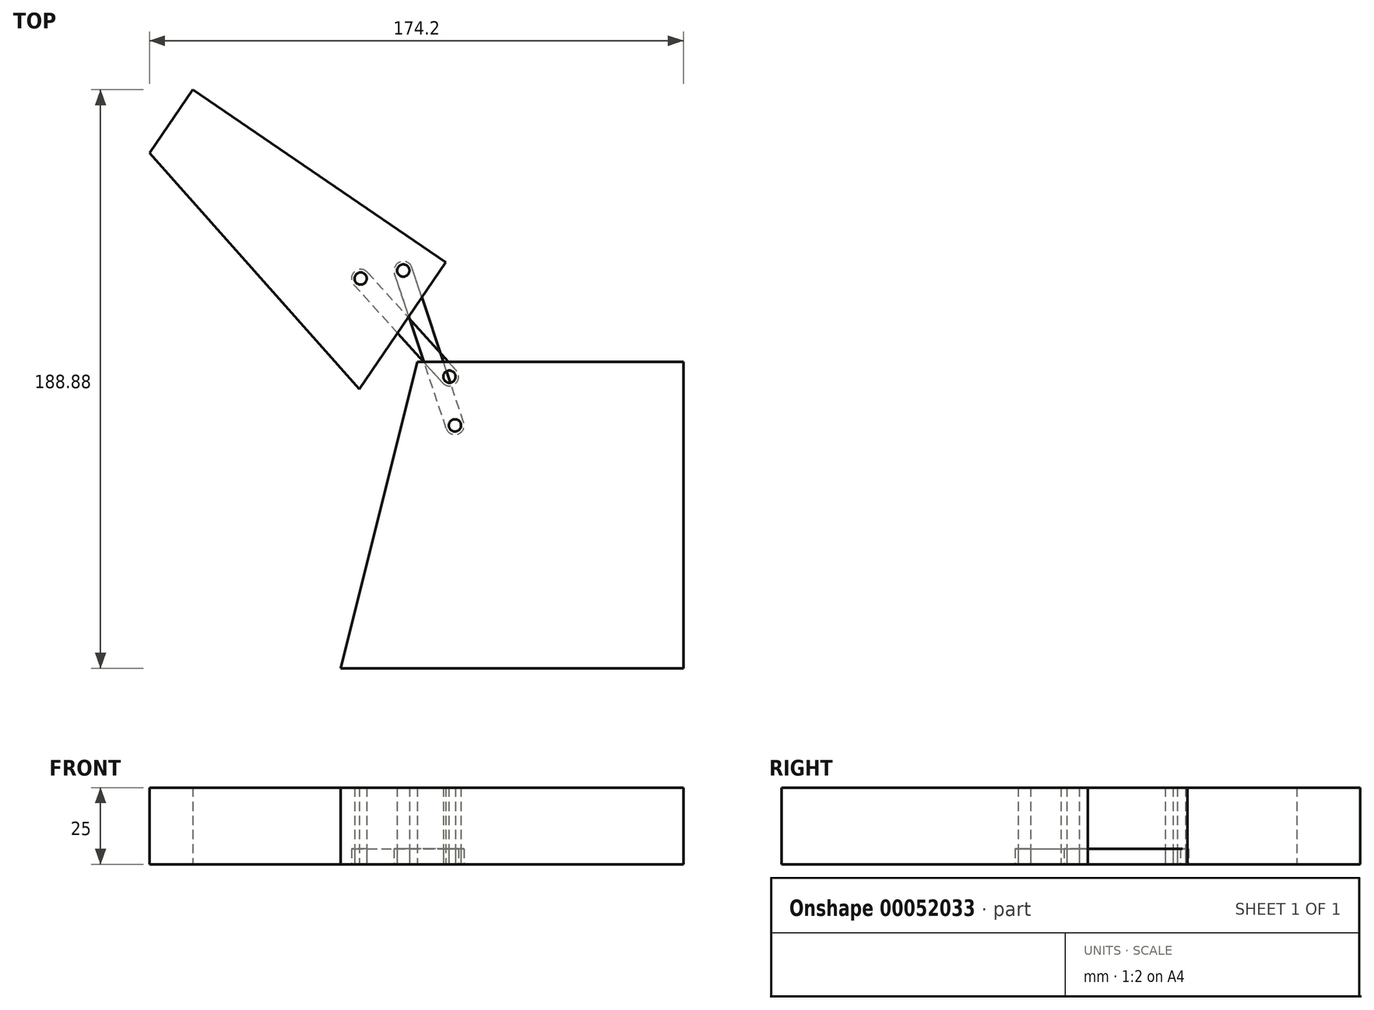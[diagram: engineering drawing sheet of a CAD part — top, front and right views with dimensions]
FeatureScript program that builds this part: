
annotation { "Feature Type Name" : "Feature", "Feature Type Description" : "" }
export const myFeature = defineFeature(function(context is Context, id is Id, definition is map)
    precondition{}
    {
        {
            var Q0;
            Q0=qCreatedBy(makeId("Top.planeOp"),FACE);
            var sketch = newSketch(context, id + "F0", { "sketchPlane" : qUnion([Q0])});
            skLineSegment(sketch, "E0.bottom", {"start": v(50, 0) * mm, "end": v(0, 0) * mm});
            skLineSegment(sketch, "E0.top", {"start": v(50, 100) * mm, "end": v(25, 100) * mm});
            skLineSegment(sketch, "E0.left", {"start": v(50, 0) * mm, "end": v(50, 100) * mm});
            skLineSegment(sketch, "E0.right", {"start": v(0, 0) * mm, "end": v(25, 100) * mm});
            skPoint(sketch, "E1", {"position": v(40, 10) * mm});
            skPoint(sketch, "E2", {"position": v(30, 20) * mm});
            skLineSegment(sketch, "E3.right", {"start": v(-34.75, -8.8) * mm, "end": v(-103.23, 68.24) * mm});
            skLineSegment(sketch, "E3.left", {"start": v(-6.55, 32.48) * mm, "end": v(-89.13, 88.88) * mm});
            skLineSegment(sketch, "E3.top", {"start": v(-89.13, 88.88) * mm, "end": v(-103.23, 68.24) * mm});
            skPoint(sketch, "E4", {"position": v(-20.45, 29.87) * mm});
            skPoint(sketch, "E5", {"position": v(-34.35, 27.25) * mm});
            skLineSegment(sketch, "E3.bottom", {"start": v(-6.55, 32.48) * mm, "end": v(-34.75, -8.8) * mm});
            skPoint(sketch, "E6", {"position": v(-55.82, -10) * mm});
            skPoint(sketch, "E7", {"position": v(-45.82, -20) * mm});
            skLineSegment(sketch, "E8.left", {"start": v(-65.82, 0) * mm, "end": v(-65.82, -100) * mm});
            skLineSegment(sketch, "E8.top", {"start": v(-65.82, -100) * mm, "end": v(-40.82, -100) * mm});
            skLineSegment(sketch, "E8.bottom", {"start": v(-65.82, 0) * mm, "end": v(-15.82, 0) * mm});
            skLineSegment(sketch, "E9", {"start": v(40, 10) * mm, "end": v(-20.45, 29.87) * mm, "construction": true});
            skLineSegment(sketch, "E10", {"start": v(-20.45, 29.87) * mm, "end": v(-55.82, -10) * mm, "construction": true});
            skLineSegment(sketch, "E11", {"start": v(30, 20) * mm, "end": v(-34.35, 27.25) * mm, "construction": true});
            skLineSegment(sketch, "E12", {"start": v(-34.35, 27.25) * mm, "end": v(-45.82, -20) * mm, "construction": true});
            skPoint(sketch, "E13", {"position": v(-38.13, 9.93) * mm});
            skPoint(sketch, "E14", {"position": v(9.78, 19.93) * mm});
            skLineSegment(sketch, "E15", {"start": v(-38.13, 9.93) * mm, "end": v(30.36, -50.84) * mm, "construction": true});
            skLineSegment(sketch, "E16", {"start": v(9.78, 19.93) * mm, "end": v(-26.41, -90.18) * mm, "construction": true});
            skPoint(sketch, "E17", {"position": v(-40.08, 3.62) * mm});
            skPoint(sketch, "E18", {"position": v(-2.17, 23.62) * mm});
            skLineSegment(sketch, "E19", {"start": v(-40.08, 3.62) * mm, "end": v(126.82, -36.9) * mm, "construction": true});
            skLineSegment(sketch, "E20", {"start": v(-2.17, 23.62) * mm, "end": v(-9.46, -41.02) * mm, "construction": true});
            skLineSegment(sketch, "E21", {"start": v(-15.82, 0) * mm, "end": v(-40.82, -100) * mm});
            skLineSegment(sketch, "E22", {"start": v(-40.82, -100) * mm, "end": v(70.97, -100) * mm});
            skLineSegment(sketch, "E23", {"start": v(70.97, -100) * mm, "end": v(70.97, 0) * mm});
            skLineSegment(sketch, "E24", {"start": v(70.97, 0) * mm, "end": v(-15.82, 0) * mm});
            skCircle(sketch, "E25", {"center": v(-20.45, 29.87) * mm, "radius": 2 * mm});
            skCircle(sketch, "E26", {"center": v(-34.35, 27.25) * mm, "radius": 3 * mm});
            skCircle(sketch, "E27", {"center": v(-20.45, 29.87) * mm, "radius": 3 * mm});
            skPoint(sketch, "E28", {"position": v(-5.38, -4.8) * mm});
            skPoint(sketch, "E29", {"position": v(-3.59, -20.72) * mm});
            skCircle(sketch, "E30", {"center": v(-34.35, 27.25) * mm, "radius": 2 * mm});
            skCircle(sketch, "E31", {"center": v(-5.38, -4.8) * mm, "radius": 2 * mm});
            skCircle(sketch, "E32", {"center": v(-5.38, -4.8) * mm, "radius": 3 * mm});
            skCircle(sketch, "E33", {"center": v(-3.59, -20.72) * mm, "radius": 2 * mm});
            skCircle(sketch, "E34", {"center": v(-3.59, -20.72) * mm, "radius": 3 * mm});
            skLineSegment(sketch, "E35", {"start": v(-36.57, 25.24) * mm, "end": v(-7.6, -6.82) * mm});
            skLineSegment(sketch, "E36", {"start": v(-32.12, 29.26) * mm, "end": v(-3.15, -2.8) * mm});
            skLineSegment(sketch, "E37", {"start": v(-0.74, -19.77) * mm, "end": v(-17.6, 30.81) * mm});
            skLineSegment(sketch, "E38", {"start": v(-6.43, -21.67) * mm, "end": v(-23.3, 28.92) * mm});
            skSolve(sketch);
        }
        {
            var Q0;
            {var subQ3=sQuery(id+"F0.wireOp",EDGE,"E21");Q0=makeQuery(id+"F0.imprint","IMPRINT",FACE,{"disambiguationData":[TD([[makeQuery(id+"F0.imprint","IMPRINT",EDGE,{"derivedFrom":subQ3}),1.0]])]});}
            var Q1;
            Q1=makeQuery(id+"F0.imprint","IMPRINT",FACE,{"disambiguationData":[TD([[makeQuery(id+"F0.imprint","IMPRINT",EDGE,{"derivedFrom":sQuery(id+"F0.wireOp",EDGE,"E33")}),-1.0]])]});
            var Q2;
            {var subQ3=sQuery(id+"F0.wireOp",EDGE,"E32");var subQ5=sQuery(id+"F0.wireOp",EDGE,"E35");var subQ6=makeQuery(id+"F0.imprint","INTERSECT",VERTEX,{"derivedFrom":[subQ3,subQ5]});Q2=makeQuery(id+"F0.imprint","IMPRINT",FACE,{"disambiguationData":[TD([[makeQuery(id+"F0.imprint","IMPRINT",EDGE,{"disambiguationData":[TD([[subQ6,-1.0]])],"derivedFrom":subQ3}),-1.0]])]});}
            var Q3;
            {var subQ0=sQuery(id+"F0.wireOp",EDGE,"E37");var subQ1=sQuery(id+"F0.wireOp",EDGE,"E31");var subQ2=makeQuery(id+"F0.imprint","INTERSECT",VERTEX,{"disambiguationData":[OD(0.0)],"derivedFrom":[subQ1,subQ0]});Q3=makeQuery(id+"F0.imprint","IMPRINT",FACE,{"disambiguationData":[TD([[makeQuery(id+"F0.imprint","IMPRINT",EDGE,{"disambiguationData":[TD([[subQ2,1.0]])],"derivedFrom":subQ1}),-1.0]])]});}
            var Q4;
            {var subQ5=sQuery(id+"F0.wireOp",EDGE,"E37");var subQ7=sQuery(id+"F0.wireOp",EDGE,"E24");var subQ8=makeQuery(id+"F0.imprint","INTERSECT",VERTEX,{"derivedFrom":[subQ7,subQ5]});Q4=makeQuery(id+"F0.imprint","IMPRINT",FACE,{"disambiguationData":[TD([[makeQuery(id+"F0.imprint","IMPRINT",EDGE,{"disambiguationData":[TD([[subQ8,-1.0]])],"derivedFrom":subQ7}),1.0]])]});}
            var Q5;
            {var subQ0=sQuery(id+"F0.wireOp",EDGE,"E36");var subQ1=sQuery(id+"F0.wireOp",EDGE,"E24");var subQ2=makeQuery(id+"F0.imprint","INTERSECT",VERTEX,{"derivedFrom":[subQ1,subQ0]});Q5=makeQuery(id+"F0.imprint","IMPRINT",FACE,{"disambiguationData":[TD([[makeQuery(id+"F0.imprint","IMPRINT",EDGE,{"disambiguationData":[TD([[subQ2,-1.0]])],"derivedFrom":subQ1}),1.0]])]});}
            var Q6;
            {var subQ0=sQuery(id+"F0.wireOp",EDGE,"E37");var subQ1=sQuery(id+"F0.wireOp",EDGE,"E31");var subQ2=makeQuery(id+"F0.imprint","INTERSECT",VERTEX,{"disambiguationData":[OD(0.0)],"derivedFrom":[subQ1,subQ0]});Q6=makeQuery(id+"F0.imprint","IMPRINT",FACE,{"disambiguationData":[TD([[makeQuery(id+"F0.imprint","IMPRINT",EDGE,{"disambiguationData":[TD([[subQ2,-1.0]])],"derivedFrom":subQ1}),-1.0]])]});}
            var Q7;
            {var subQ0=sQuery(id+"F0.wireOp",EDGE,"E38");var subQ1=sQuery(id+"F0.wireOp",EDGE,"E24");var subQ2=makeQuery(id+"F0.imprint","INTERSECT",VERTEX,{"derivedFrom":[subQ1,subQ0]});Q7=makeQuery(id+"F0.imprint","IMPRINT",FACE,{"disambiguationData":[TD([[makeQuery(id+"F0.imprint","IMPRINT",EDGE,{"disambiguationData":[TD([[subQ2,-1.0]])],"derivedFrom":subQ1}),1.0]])]});}
            extrude(context, id + "F1", {"entities" : qUnion([Q0, Q1, Q2, Q3, Q4, Q5, Q6, Q7]), "depth" : 25 * mm});
        }
        {
            var Q0;
            {var subQ15=sQuery(id+"F0.wireOp",EDGE,"E3.left");Q0=makeQuery(id+"F0.imprint","IMPRINT",FACE,{"disambiguationData":[TD([[makeQuery(id+"F0.imprint","IMPRINT",EDGE,{"derivedFrom":subQ15}),1.0]])]});}
            var Q1;
            {var subQ0=sQuery(id+"F0.wireOp",EDGE,"E36");var subQ1=sQuery(id+"F0.wireOp",EDGE,"E3.bottom");var subQ2=makeQuery(id+"F0.imprint","INTERSECT",VERTEX,{"derivedFrom":[subQ1,subQ0]});Q1=makeQuery(id+"F0.imprint","IMPRINT",FACE,{"disambiguationData":[TD([[makeQuery(id+"F0.imprint","IMPRINT",EDGE,{"disambiguationData":[TD([[subQ2,-1.0]])],"derivedFrom":subQ1}),-1.0]])]});}
            var Q2;
            {var subQ0=sQuery(id+"F0.wireOp",EDGE,"E3.bottom");var subQ1=sQuery(id+"F0.wireOp",EDGE,"E3.right");var subQ2=makeQuery(id+"F0.imprint","INTERSECT",VERTEX,{"derivedFrom":[subQ1,subQ0]});Q2=makeQuery(id+"F0.imprint","IMPRINT",FACE,{"disambiguationData":[TD([[makeQuery(id+"F0.imprint","IMPRINT",EDGE,{"disambiguationData":[TD([[subQ2,-1.0]])],"derivedFrom":subQ1}),-1.0]])]});}
            var Q3;
            {var subQ0=sQuery(id+"F0.wireOp",EDGE,"E37");var subQ1=sQuery(id+"F0.wireOp",EDGE,"E3.bottom");var subQ2=makeQuery(id+"F0.imprint","INTERSECT",VERTEX,{"derivedFrom":[subQ1,subQ0]});Q3=makeQuery(id+"F0.imprint","IMPRINT",FACE,{"disambiguationData":[TD([[makeQuery(id+"F0.imprint","IMPRINT",EDGE,{"disambiguationData":[TD([[subQ2,-1.0]])],"derivedFrom":subQ1}),-1.0]])]});}
            var Q4;
            Q4=makeQuery(id+"F0.imprint","IMPRINT",FACE,{"disambiguationData":[TD([[makeQuery(id+"F0.imprint","IMPRINT",EDGE,{"derivedFrom":sQuery(id+"F0.wireOp",EDGE,"E25")}),-1.0]])]});
            var Q5;
            Q5=makeQuery(id+"F0.imprint","IMPRINT",FACE,{"disambiguationData":[TD([[makeQuery(id+"F0.imprint","IMPRINT",EDGE,{"derivedFrom":sQuery(id+"F0.wireOp",EDGE,"E30")}),-1.0]])]});
            extrude(context, id + "F2", {"entities" : qUnion([Q0, Q1, Q2, Q3, Q4, Q5]), "depth" : 25 * mm});
        }
        {
            var Q0;
            {var subQ0=sQuery(id+"F0.wireOp",EDGE,"E37");var subQ1=sQuery(id+"F0.wireOp",EDGE,"E3.bottom");var subQ2=makeQuery(id+"F0.imprint","INTERSECT",VERTEX,{"derivedFrom":[subQ1,subQ0]});Q0=makeQuery(id+"F0.imprint","IMPRINT",FACE,{"disambiguationData":[TD([[makeQuery(id+"F0.imprint","IMPRINT",EDGE,{"disambiguationData":[TD([[subQ2,-1.0]])],"derivedFrom":subQ1}),-1.0]])]});}
            var Q1;
            {var subQ0=sQuery(id+"F0.wireOp",EDGE,"E37");var subQ1=sQuery(id+"F0.wireOp",EDGE,"E3.bottom");var subQ2=makeQuery(id+"F0.imprint","INTERSECT",VERTEX,{"derivedFrom":[subQ1,subQ0]});Q1=makeQuery(id+"F0.imprint","IMPRINT",FACE,{"disambiguationData":[TD([[makeQuery(id+"F0.imprint","IMPRINT",EDGE,{"disambiguationData":[TD([[subQ2,-1.0]])],"derivedFrom":subQ1}),1.0]])]});}
            var Q2;
            {var subQ0=sQuery(id+"F0.wireOp",EDGE,"E37");var subQ1=sQuery(id+"F0.wireOp",EDGE,"E24");var subQ2=makeQuery(id+"F0.imprint","INTERSECT",VERTEX,{"derivedFrom":[subQ1,subQ0]});Q2=makeQuery(id+"F0.imprint","IMPRINT",FACE,{"disambiguationData":[TD([[makeQuery(id+"F0.imprint","IMPRINT",EDGE,{"disambiguationData":[TD([[subQ2,-1.0]])],"derivedFrom":subQ1}),-1.0]])]});}
            var Q3;
            {var subQ5=sQuery(id+"F0.wireOp",EDGE,"E37");var subQ7=sQuery(id+"F0.wireOp",EDGE,"E24");var subQ8=makeQuery(id+"F0.imprint","INTERSECT",VERTEX,{"derivedFrom":[subQ7,subQ5]});Q3=makeQuery(id+"F0.imprint","IMPRINT",FACE,{"disambiguationData":[TD([[makeQuery(id+"F0.imprint","IMPRINT",EDGE,{"disambiguationData":[TD([[subQ8,-1.0]])],"derivedFrom":subQ7}),1.0]])]});}
            var Q4;
            {var subQ3=sQuery(id+"F0.wireOp",EDGE,"E32");var subQ5=sQuery(id+"F0.wireOp",EDGE,"E35");var subQ6=makeQuery(id+"F0.imprint","INTERSECT",VERTEX,{"derivedFrom":[subQ3,subQ5]});Q4=makeQuery(id+"F0.imprint","IMPRINT",FACE,{"disambiguationData":[TD([[makeQuery(id+"F0.imprint","IMPRINT",EDGE,{"disambiguationData":[TD([[subQ6,-1.0]])],"derivedFrom":subQ3}),-1.0]])]});}
            var Q5;
            Q5=makeQuery(id+"F0.imprint","IMPRINT",FACE,{"disambiguationData":[TD([[makeQuery(id+"F0.imprint","IMPRINT",EDGE,{"derivedFrom":sQuery(id+"F0.wireOp",EDGE,"E33")}),-1.0]])]});
            var Q6;
            Q6=makeQuery(id+"F0.imprint","IMPRINT",FACE,{"disambiguationData":[TD([[makeQuery(id+"F0.imprint","IMPRINT",EDGE,{"derivedFrom":sQuery(id+"F0.wireOp",EDGE,"E25")}),-1.0]])]});
            var Q7;
            {var subQ0=sQuery(id+"F0.wireOp",EDGE,"E37");var subQ1=sQuery(id+"F0.wireOp",EDGE,"E31");var subQ2=makeQuery(id+"F0.imprint","INTERSECT",VERTEX,{"disambiguationData":[OD(0.0)],"derivedFrom":[subQ1,subQ0]});Q7=makeQuery(id+"F0.imprint","IMPRINT",FACE,{"disambiguationData":[TD([[makeQuery(id+"F0.imprint","IMPRINT",EDGE,{"disambiguationData":[TD([[subQ2,1.0]])],"derivedFrom":subQ1}),-1.0]])]});}
            var Q8;
            {var subQ0=sQuery(id+"F0.wireOp",EDGE,"E37");var subQ1=sQuery(id+"F0.wireOp",EDGE,"E31");var subQ2=makeQuery(id+"F0.imprint","INTERSECT",VERTEX,{"disambiguationData":[OD(0.0)],"derivedFrom":[subQ1,subQ0]});Q8=makeQuery(id+"F0.imprint","IMPRINT",FACE,{"disambiguationData":[TD([[makeQuery(id+"F0.imprint","IMPRINT",EDGE,{"disambiguationData":[TD([[subQ2,1.0]])],"derivedFrom":subQ1}),1.0]])]});}
            extrude(context, id + "F3", {"entities" : qUnion([Q0, Q1, Q2, Q3, Q4, Q5, Q6, Q7, Q8]), "depth" : 5 * mm});
        }
        {
            var Q0;
            {var subQ0=sQuery(id+"F0.wireOp",EDGE,"E37");var subQ1=sQuery(id+"F0.wireOp",EDGE,"E24");var subQ2=makeQuery(id+"F0.imprint","INTERSECT",VERTEX,{"derivedFrom":[subQ1,subQ0]});Q0=makeQuery(id+"F0.imprint","IMPRINT",FACE,{"disambiguationData":[TD([[makeQuery(id+"F0.imprint","IMPRINT",EDGE,{"disambiguationData":[TD([[subQ2,-1.0]])],"derivedFrom":subQ1}),-1.0]])]});}
            var Q1;
            {var subQ0=sQuery(id+"F0.wireOp",EDGE,"E36");var subQ1=sQuery(id+"F0.wireOp",EDGE,"E3.bottom");var subQ2=makeQuery(id+"F0.imprint","INTERSECT",VERTEX,{"derivedFrom":[subQ1,subQ0]});Q1=makeQuery(id+"F0.imprint","IMPRINT",FACE,{"disambiguationData":[TD([[makeQuery(id+"F0.imprint","IMPRINT",EDGE,{"disambiguationData":[TD([[subQ2,-1.0]])],"derivedFrom":subQ1}),1.0]])]});}
            var Q2;
            {var subQ5=sQuery(id+"F0.wireOp",EDGE,"E37");var subQ7=sQuery(id+"F0.wireOp",EDGE,"E24");var subQ8=makeQuery(id+"F0.imprint","INTERSECT",VERTEX,{"derivedFrom":[subQ7,subQ5]});Q2=makeQuery(id+"F0.imprint","IMPRINT",FACE,{"disambiguationData":[TD([[makeQuery(id+"F0.imprint","IMPRINT",EDGE,{"disambiguationData":[TD([[subQ8,-1.0]])],"derivedFrom":subQ7}),1.0]])]});}
            var Q3;
            {var subQ0=sQuery(id+"F0.wireOp",EDGE,"E38");var subQ1=sQuery(id+"F0.wireOp",EDGE,"E24");var subQ2=makeQuery(id+"F0.imprint","INTERSECT",VERTEX,{"derivedFrom":[subQ1,subQ0]});Q3=makeQuery(id+"F0.imprint","IMPRINT",FACE,{"disambiguationData":[TD([[makeQuery(id+"F0.imprint","IMPRINT",EDGE,{"disambiguationData":[TD([[subQ2,-1.0]])],"derivedFrom":subQ1}),1.0]])]});}
            var Q4;
            {var subQ0=sQuery(id+"F0.wireOp",EDGE,"E36");var subQ1=sQuery(id+"F0.wireOp",EDGE,"E24");var subQ2=makeQuery(id+"F0.imprint","INTERSECT",VERTEX,{"derivedFrom":[subQ1,subQ0]});Q4=makeQuery(id+"F0.imprint","IMPRINT",FACE,{"disambiguationData":[TD([[makeQuery(id+"F0.imprint","IMPRINT",EDGE,{"disambiguationData":[TD([[subQ2,-1.0]])],"derivedFrom":subQ1}),1.0]])]});}
            var Q5;
            {var subQ0=sQuery(id+"F0.wireOp",EDGE,"E37");var subQ1=sQuery(id+"F0.wireOp",EDGE,"E31");var subQ2=makeQuery(id+"F0.imprint","INTERSECT",VERTEX,{"disambiguationData":[OD(0.0)],"derivedFrom":[subQ1,subQ0]});Q5=makeQuery(id+"F0.imprint","IMPRINT",FACE,{"disambiguationData":[TD([[makeQuery(id+"F0.imprint","IMPRINT",EDGE,{"disambiguationData":[TD([[subQ2,1.0]])],"derivedFrom":subQ1}),-1.0]])]});}
            var Q6;
            {var subQ0=sQuery(id+"F0.wireOp",EDGE,"E37");var subQ1=sQuery(id+"F0.wireOp",EDGE,"E31");var subQ2=makeQuery(id+"F0.imprint","INTERSECT",VERTEX,{"disambiguationData":[OD(0.0)],"derivedFrom":[subQ1,subQ0]});Q6=makeQuery(id+"F0.imprint","IMPRINT",FACE,{"disambiguationData":[TD([[makeQuery(id+"F0.imprint","IMPRINT",EDGE,{"disambiguationData":[TD([[subQ2,-1.0]])],"derivedFrom":subQ1}),-1.0]])]});}
            var Q7;
            {var subQ0=sQuery(id+"F0.wireOp",EDGE,"E36");var subQ1=sQuery(id+"F0.wireOp",EDGE,"E3.bottom");var subQ2=makeQuery(id+"F0.imprint","INTERSECT",VERTEX,{"derivedFrom":[subQ1,subQ0]});Q7=makeQuery(id+"F0.imprint","IMPRINT",FACE,{"disambiguationData":[TD([[makeQuery(id+"F0.imprint","IMPRINT",EDGE,{"disambiguationData":[TD([[subQ2,-1.0]])],"derivedFrom":subQ1}),-1.0]])]});}
            var Q8;
            Q8=makeQuery(id+"F0.imprint","IMPRINT",FACE,{"disambiguationData":[TD([[makeQuery(id+"F0.imprint","IMPRINT",EDGE,{"derivedFrom":sQuery(id+"F0.wireOp",EDGE,"E30")}),-1.0]])]});
            var Q9;
            {var subQ0=sQuery(id+"F0.wireOp",EDGE,"E36");var subQ1=sQuery(id+"F0.wireOp",EDGE,"E24");var subQ2=makeQuery(id+"F0.imprint","INTERSECT",VERTEX,{"derivedFrom":[subQ1,subQ0]});Q9=makeQuery(id+"F0.imprint","IMPRINT",FACE,{"disambiguationData":[TD([[makeQuery(id+"F0.imprint","IMPRINT",EDGE,{"disambiguationData":[TD([[subQ2,-1.0]])],"derivedFrom":subQ1}),-1.0]])]});}
            extrude(context, id + "F4", {"entities" : qUnion([Q0, Q1, Q2, Q3, Q4, Q5, Q6, Q7, Q8, Q9]), "depth" : 5 * mm});
        }
    });
